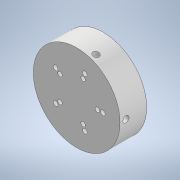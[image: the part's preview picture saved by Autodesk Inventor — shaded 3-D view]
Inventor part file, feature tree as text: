
AUTODESK INVENTOR PART (.ipt)
format: ipt  version: 2022 (Build 260153000, 153)  size: 346,112 bytes
history: native  units: mm
features: other x6, sketch x5, extrude x4, pattern_circular x3, reference x3, plane x1, sweep x1
ambient origin geometry x8: Origin, YZ Plane, XZ Plane, XY Plane, X Axis, Y Axis, Z Axis, Center Point
bodies: Solid1 (feature_tree)
feature tree (23):
  extrude  "Extrusion1"  Depth=38.798324mm
  plane  "Work Plane1"
  extrude  "Extrusion2"  Depth=20.0mm TaperAngle=360.0deg
  pattern_circular  "Circular Pattern1"  Count=5 Angle=360.0deg
  extrude  "Extrusion3"  Depth=20.0mm TaperAngle=0.0deg
  sweep  "Sweep1"
  pattern_circular  "Circular Pattern2"  [2 undecoded]
  extrude  "Extrusion4"  TaperAngle=0.0deg  [1 undecoded]
  pattern_circular  "Circular Pattern3"  Count=5 Angle=360.0deg
  sketch  "Sketch1"  dims[d0=28.798324mm d1=38.798324mm]
  reference  "Reference1"
  sketch  "Sketch2"  dims[d2=20.0mm d3=50.0mm d5=360.0deg]
  reference  "Reference2"
  reference  "Reference3"
  sketch  "Sketch4"  dims[d7=1.0mm d8=9.0mm d9=0.0mm d10=0.0mm]
  sketch  "Sketch5"  dims[d11=1.0mm d12=0.0mm d13=50.0mm d14=360.0deg]
  sketch  "Sketch6"  dims[d16=50.0mm d18=360.0deg d20=20.0mm d21=0.0mm d22=7.0mm d23=3.5mm d24=0.0mm d25=0.0mm d26=50.0mm d27=360.0deg d29=5.0mm d30=0.0mm d31=0.0mm d32=50.0mm d33=360.0deg]
  other  "<userpath>\OneDrive - Imperial College London\ROBOICP\new vial holder assembly.iam"
  other  "new vial holder assembly.iam"
  other  "vial thread insert:1"
  other  "vial:1"
  other  "mixer_gear:1"
  other  "Assembly1"
note: 3 required parameter values undecoded (feature->parameter linkage not recoverable at this tier; creation-order binding heuristic only, values carry confidence <= 0.55)
